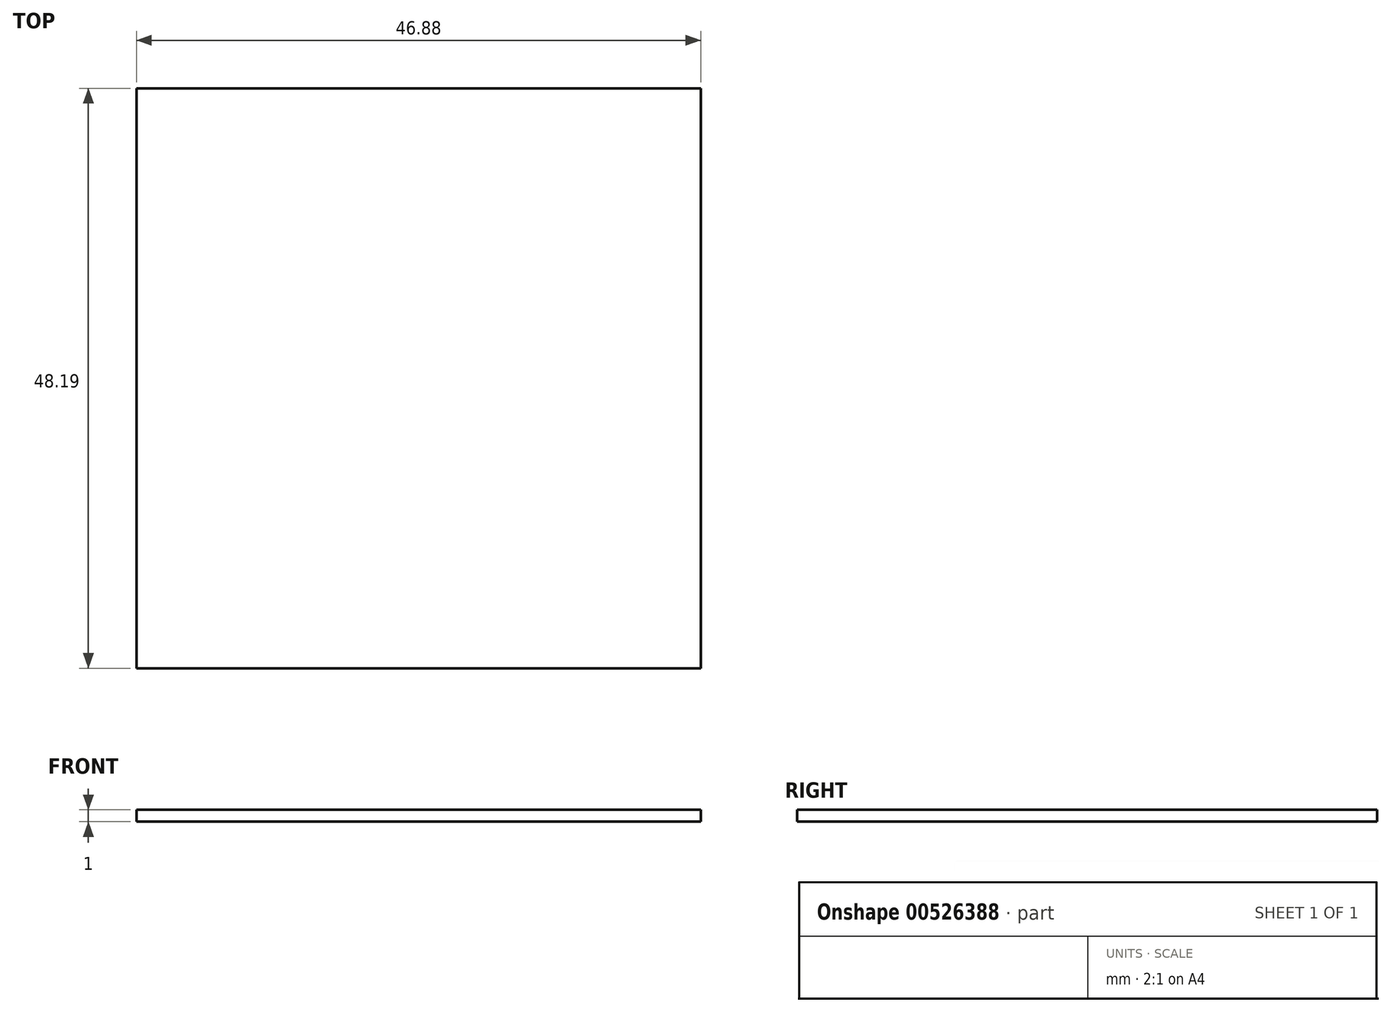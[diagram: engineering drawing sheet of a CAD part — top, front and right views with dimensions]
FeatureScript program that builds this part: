
annotation { "Feature Type Name" : "Feature", "Feature Type Description" : "" }
export const myFeature = defineFeature(function(context is Context, id is Id, definition is map)
    precondition{}
    {
        {
            var Q0;
            Q0=qCreatedBy(makeId("Top.planeOp"),FACE);
            var sketch = newSketch(context, id + "F0", { "sketchPlane" : qUnion([Q0])});
            skLineSegment(sketch, "E0.bottom", {"start": v(-27.49, 35.56) * mm, "end": v(19.39, 35.56) * mm});
            skLineSegment(sketch, "E0.top", {"start": v(-27.49, -12.63) * mm, "end": v(19.39, -12.63) * mm});
            skLineSegment(sketch, "E0.left", {"start": v(-27.49, 35.56) * mm, "end": v(-27.49, -12.63) * mm});
            skLineSegment(sketch, "E0.right", {"start": v(19.39, 35.56) * mm, "end": v(19.39, -12.63) * mm});
            skSolve(sketch);
        }
        {
            var Q0;
            Q0=makeQuery(id+"F0.imprint","IMPRINT",FACE,{"disambiguationData":[TD([[makeQuery(id+"F0.imprint","IMPRINT",EDGE,{"derivedFrom":sQuery(id+"F0.wireOp",EDGE,"E0.bottom")}),-1.0]])]});
            var Q1;
            Q1 = qSketchRegion(id + "F0", true);
            var Q2;
            Q2=sQuery(id+"F0.wireOp",EDGE,"E0.right");
            var Q3;
            Q3=sQuery(id+"F0.wireOp",EDGE,"E0.bottom");
            var Q4;
            Q4=sQuery(id+"F0.wireOp",EDGE,"E0.left");
            var Q5;
            Q5=sQuery(id+"F0.wireOp",EDGE,"E0.top");
            extrude(context, id + "F1", {"entities" : qUnion([Q0, Q1]), "bodyType" : ToolBodyType.SURFACE, "surfaceEntities" : qUnion([Q2, Q3, Q4, Q5]), "endBound" : BoundingType.SYMMETRIC, "depth" : 1 * mm, "offsetDistance" : 25.4 * mm});
        }
    });
